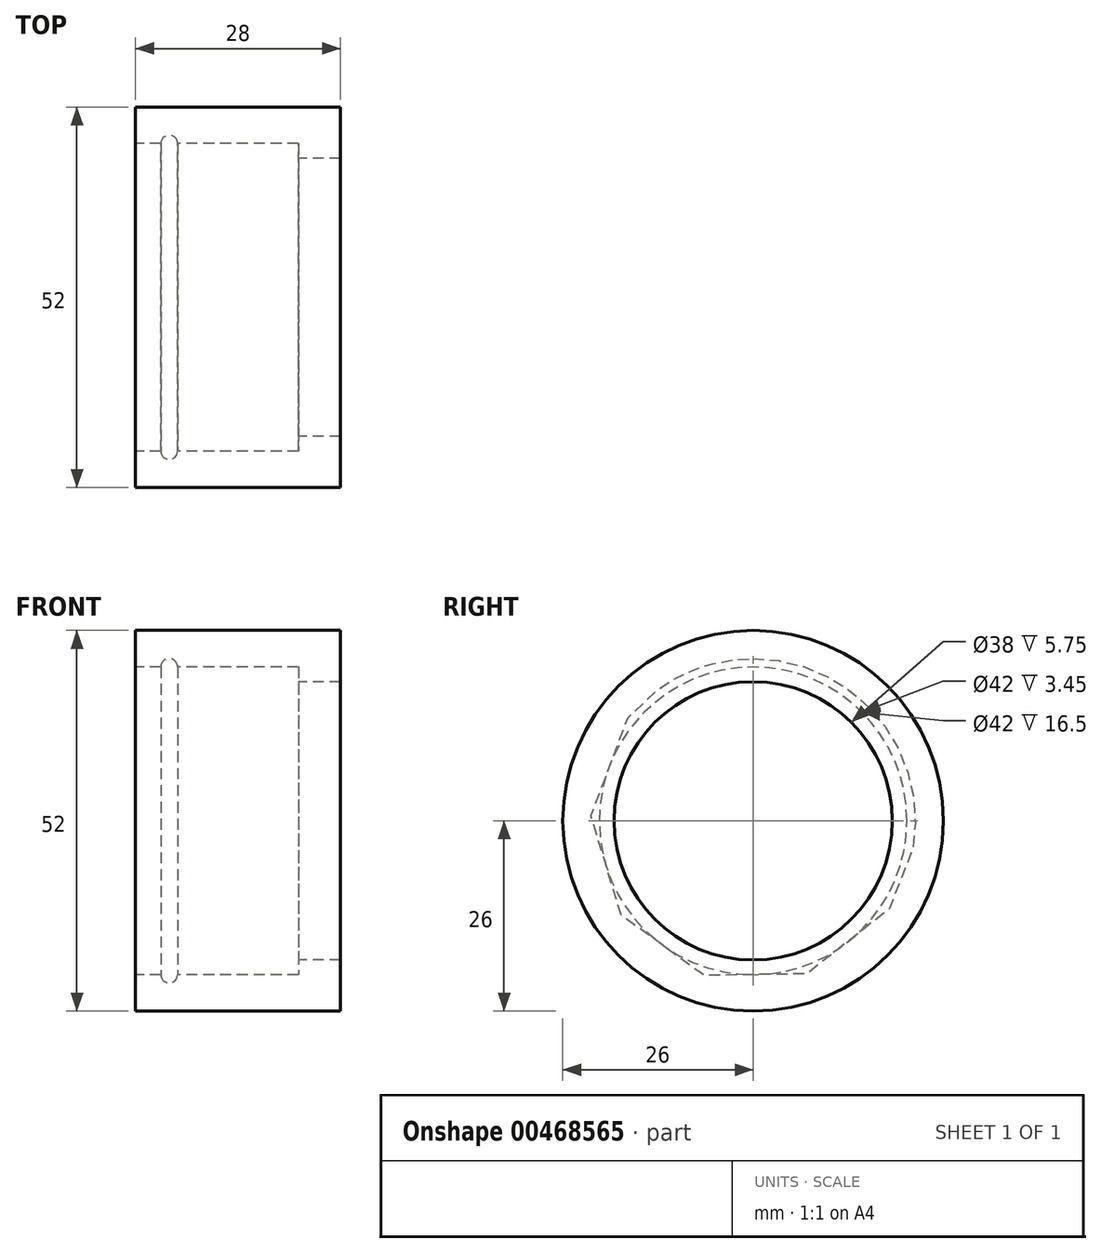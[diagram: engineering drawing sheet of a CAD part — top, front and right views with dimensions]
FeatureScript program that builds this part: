
annotation { "Feature Type Name" : "Feature", "Feature Type Description" : "" }
export const myFeature = defineFeature(function(context is Context, id is Id, definition is map)
    precondition{}
    {
        {
            var Q0;
            Q0=qCreatedBy(makeId("Front.planeOp"),FACE);
            var sketch = newSketch(context, id + "F0", { "sketchPlane" : qUnion([Q0])});
            skLineSegment(sketch, "E0", {"start": v(0, 0) * mm, "end": v(28, 0) * mm});
            skPoint(sketch, "E1", {"position": v(14, 0) * mm});
            skPoint(sketch, "E2", {"position": v(14, 21) * mm});
            skLineSegment(sketch, "E3", {"start": v(14, 21) * mm, "end": v(22.25, 21) * mm});
            skLineSegment(sketch, "E4", {"start": v(14, 21) * mm, "end": v(5.75, 21) * mm});
            skPoint(sketch, "E5", {"position": v(4.6, 21) * mm});
            skCircle(sketch, "E6", {"center": v(4.6, 21) * mm, "radius": 1.15 * mm});
            skPoint(sketch, "E7", {"position": v(0, 21) * mm});
            skLineSegment(sketch, "E8", {"start": v(0, 21) * mm, "end": v(3.45, 21) * mm});
            skLineSegment(sketch, "E9", {"start": v(3.45, 21) * mm, "end": v(5.75, 21) * mm});
            skLineSegment(sketch, "E10", {"start": v(0, 21) * mm, "end": v(0, 26) * mm});
            skLineSegment(sketch, "E11", {"start": v(22.25, 21) * mm, "end": v(22.25, 19) * mm});
            skLineSegment(sketch, "E12", {"start": v(22.25, 19) * mm, "end": v(28, 19) * mm});
            skLineSegment(sketch, "E13", {"start": v(28, 19) * mm, "end": v(28, 26) * mm});
            skLineSegment(sketch, "E14", {"start": v(28, 26) * mm, "end": v(0, 26) * mm});
            skSolve(sketch);
        }
        {
            var Q0;
            Q0=makeQuery(id+"F0.imprint","IMPRINT",FACE,{"disambiguationData":[TD([[makeQuery(id+"F0.imprint","IMPRINT",EDGE,{"derivedFrom":sQuery(id+"F0.wireOp",EDGE,"E3")}),1.0]])]});
            var Q1;
            Q1=sQuery(id+"F0.wireOp",EDGE,"E0");
            revolve(context, id + "F1", {"surfaceOperationType" : NewSurfaceOperationType.NEW, "entities" : qUnion([Q0]), "axis" : qUnion([Q1]), "revolveType" : RevolveType.FULL});
        }
    });
